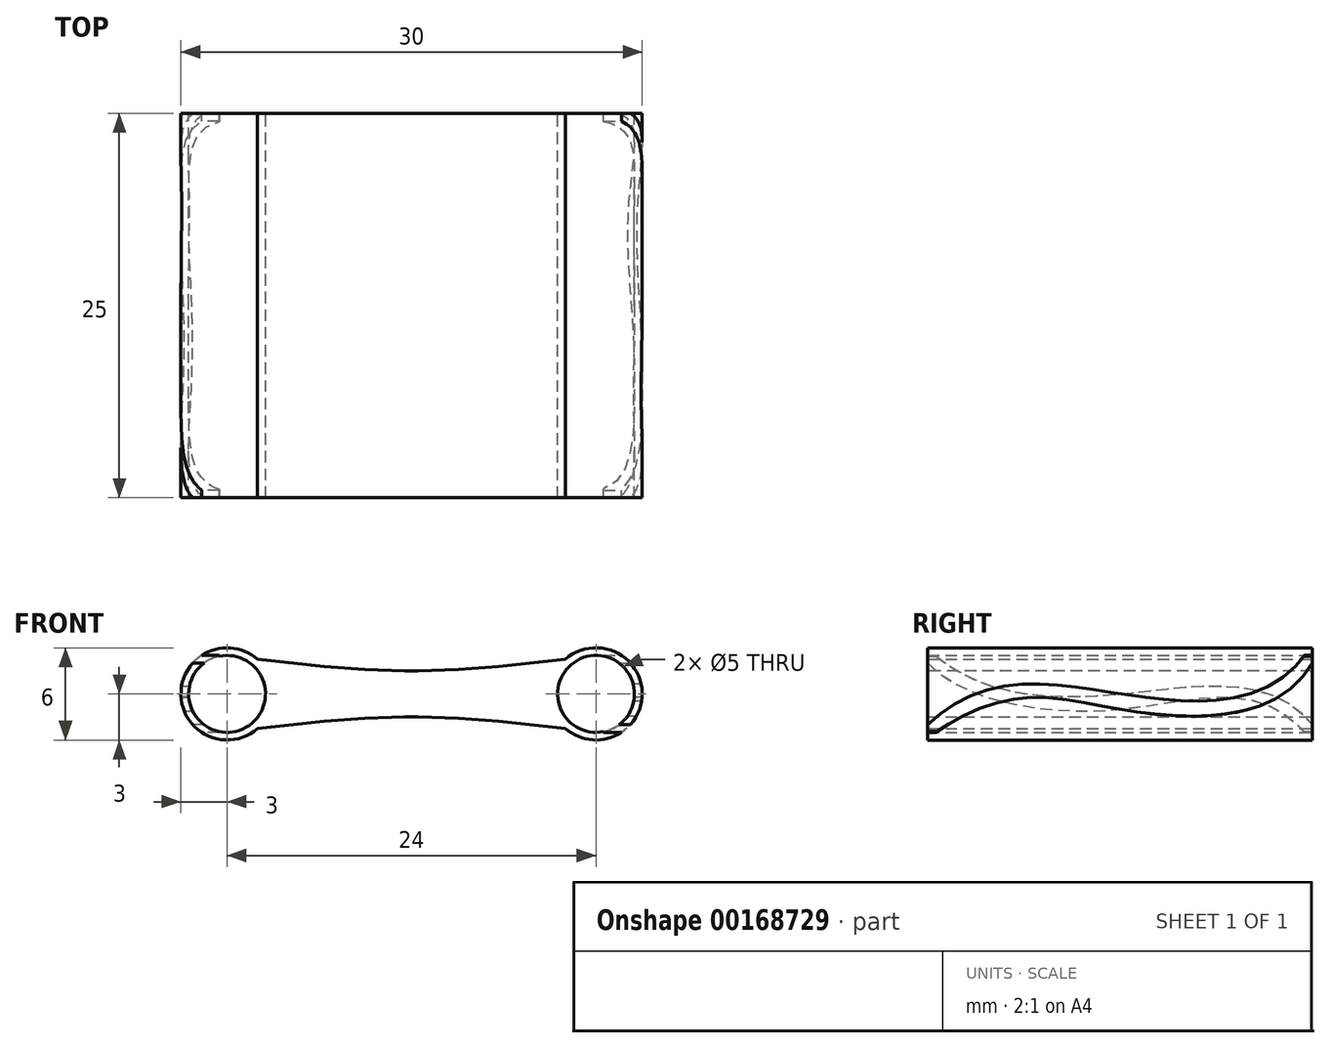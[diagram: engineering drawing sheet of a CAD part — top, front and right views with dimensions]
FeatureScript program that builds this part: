
annotation { "Feature Type Name" : "Feature", "Feature Type Description" : "" }
export const myFeature = defineFeature(function(context is Context, id is Id, definition is map)
    precondition{}
    {
        {
            var Q0;
            Q0=qCreatedBy(makeId("Front.planeOp"),FACE);
            var sketch = newSketch(context, id + "F0", { "sketchPlane" : qUnion([Q0])});
            skPoint(sketch, "E0.middle", {"position": v(0, 0) * mm});
            skCircle(sketch, "E1", {"center": v(12, 0) * mm, "radius": 3 * mm});
            skCircle(sketch, "E2", {"center": v(-12, 0) * mm, "radius": 3 * mm});
            skLineSegment(sketch, "E3", {"start": v(-12, 0) * mm, "end": v(12, 0) * mm, "construction": true});
            skLineSegment(sketch, "E4", {"start": v(-4.98, -1.5) * mm, "end": v(5.72, -1.5) * mm, "construction": true});
            skPoint(sketch, "E5.1.internal.snap0", {"position": v(0.37, -1.5) * mm});
            skLineSegment(sketch, "E6", {"start": v(-10.93, -2.25) * mm, "end": v(10.8, -2.25) * mm, "construction": true});
            skFitSpline(sketch, "E7", {"points": [v(-10.02, -2.25) * mm, v(0, -1.5) * mm, v(10.02, -2.25) * mm], "startDerivative": vector(20.04, 2.26) * mm, "endDerivative": vector(20.04, -2.26) * mm});
            skLineSegment(sketch, "E8", {"start": v(-10.93, 2.25) * mm, "end": v(10.8, 2.25) * mm, "construction": true});
            skLineSegment(sketch, "E9", {"start": v(-4.98, 1.5) * mm, "end": v(5.72, 1.5) * mm, "construction": true});
            skFitSpline(sketch, "E10", {"points": [v(-10.02, 2.25) * mm, v(0, 1.5) * mm, v(10.02, 2.25) * mm], "startDerivative": vector(20.03, -2.25) * mm, "endDerivative": vector(20.03, 2.25) * mm});
            skCircle(sketch, "E11", {"center": v(-12, 0) * mm, "radius": 2.5 * mm});
            skCircle(sketch, "E12", {"center": v(12, 0) * mm, "radius": 2.5 * mm});
            skSolve(sketch);
        }
        {
            var Q0;
            {var subQ0=sQuery(id+"F0.wireOp",EDGE,"E2");var subQ1=sQuery(id+"F0.wireOp",EDGE,"E0.bottom");var subQ2=makeQuery(id+"F0.imprint","INTERSECT",VERTEX,{"derivedFrom":[subQ1,subQ0]});Q0=makeQuery(id+"F0.imprint","IMPRINT",FACE,{"disambiguationData":[TD([[makeQuery(id+"F0.imprint","IMPRINT",EDGE,{"disambiguationData":[TD([[subQ2,-1.0]])],"derivedFrom":subQ1}),-1.0]])]});}
            var Q1;
            {var subQ0=sQuery(id+"F0.wireOp",EDGE,"E7");Q1=makeQuery(id+"F0.imprint","IMPRINT",FACE,{"disambiguationData":[TD([[makeQuery(id+"F0.imprint","IMPRINT",EDGE,{"derivedFrom":subQ0}),1.0]])]});}
            var Q2;
            {var subQ0=sQuery(id+"F0.wireOp",EDGE,"E2");var subQ1=makeQuery(id+"F0.imprint","INTERSECT",VERTEX,{"derivedFrom":[subQ0,sQuery(id+"F0.wireOp",EDGE,"E7")]});Q2=makeQuery(id+"F0.imprint","IMPRINT",FACE,{"disambiguationData":[TD([[makeQuery(id+"F0.imprint","IMPRINT",EDGE,{"disambiguationData":[TD([[subQ1,1.0]])],"derivedFrom":subQ0}),1.0]])]});}
            var Q3;
            {var subQ0=sQuery(id+"F0.wireOp",EDGE,"E1");var subQ1=makeQuery(id+"F0.imprint","INTERSECT",VERTEX,{"derivedFrom":[subQ0,sQuery(id+"F0.wireOp",EDGE,"E7")]});Q3=makeQuery(id+"F0.imprint","IMPRINT",FACE,{"disambiguationData":[TD([[makeQuery(id+"F0.imprint","IMPRINT",EDGE,{"disambiguationData":[TD([[subQ1,1.0]])],"derivedFrom":subQ0}),1.0]])]});}
            extrude(context, id + "F1", {"entities" : qUnion([Q0, Q1, Q2, Q3]), "depth" : 25 * mm, "offsetDistance" : 25 * mm, "symmetric" : true});
        }
        {
            var Q0;
            Q0=qCreatedBy(makeId("Right.planeOp"),FACE);
            var sketch = newSketch(context, id + "F2", { "sketchPlane" : qUnion([Q0])});
            skSolve(sketch);
        }
        {
            var Q0;
            Q0 = qBodyType(qCreatedBy(id + "F2" ,EDGE), BodyType.WIRE);
            var Q1;
            Q1=qCreatedBy(makeId("Right.planeOp"),FACE);
            cPlane(context, id + "F3", {"entities" : qUnion([Q0, Q1]), "cplaneType" : CPlaneType.OFFSET, "offset" : 15 * mm, "width" : 150 * mm, "height" : 150 * mm});
        }
        {
            var Q0;
            Q0=qCreatedBy(id+"F3.planeOp",FACE);
            var sketch = newSketch(context, id + "F4", { "sketchPlane" : qUnion([Q0])});
            skFitSpline(sketch, "E13", {"points": [v(-12.5, -2) * mm, v(0, 0) * mm, v(12.03, 2.54) * mm], "startDerivative": vector(22.83, 21.55) * mm, "endDerivative": vector(16.38, 22.12) * mm});
            skFitSpline(sketch, "E14", {"points": [v(-12, -2.5) * mm, v(0, -1) * mm, v(12.5, 2) * mm], "startDerivative": vector(30.94, 20.46) * mm, "endDerivative": vector(13.56, 23.82) * mm});
            skLineSegment(sketch, "E15.bottom", {"start": v(-12.5, 2.5) * mm, "end": v(12.5, 2.5) * mm});
            skLineSegment(sketch, "E15.top", {"start": v(-12.5, -2.5) * mm, "end": v(12.5, -2.5) * mm});
            skLineSegment(sketch, "E15.left", {"start": v(-12.5, 2.5) * mm, "end": v(-12.5, -2.5) * mm});
            skLineSegment(sketch, "E15.right", {"start": v(12.5, 2.5) * mm, "end": v(12.5, -2.5) * mm});
            skSolve(sketch);
        }
        {
            var Q0;
            {var subQ5=sQuery(id+"F4.wireOp",EDGE,"E13");Q0=makeQuery(id+"F4.imprint","IMPRINT",FACE,{"disambiguationData":[TD([[makeQuery(id+"F4.imprint","IMPRINT",EDGE,{"derivedFrom":subQ5}),-1.0]])]});}
            extrude(context, id + "F5", {"entities" : qUnion([Q0]), "operationType" : NewBodyOperationType.REMOVE, "oppositeDirection" : true, "depth" : 5 * mm, "offsetDistance" : 25 * mm, "symmetric" : true});
        }
        {
            var Q0;
            Q0=qCreatedBy(makeId("Right.planeOp"),FACE);
            var sketch = newSketch(context, id + "F6", { "sketchPlane" : qUnion([Q0])});
            skSolve(sketch);
        }
        {
            var Q0;
            Q0 = qBodyType(qCreatedBy(id + "F6" ,EDGE), BodyType.WIRE);
            var Q1;
            Q1=qCreatedBy(makeId("Right.planeOp"),FACE);
            cPlane(context, id + "F7", {"entities" : qUnion([Q0, Q1]), "cplaneType" : CPlaneType.OFFSET, "offset" : 15 * mm, "oppositeDirection" : true, "width" : 150 * mm, "height" : 150 * mm});
        }
        {
            var Q0;
            Q0=qCreatedBy(id+"F7.planeOp",FACE);
            var sketch = newSketch(context, id + "F8", { "sketchPlane" : qUnion([Q0])});
            skLineSegment(sketch, "E16.bottom", {"start": v(12.5, 2.5) * mm, "end": v(-12.5, 2.5) * mm});
            skLineSegment(sketch, "E16.top", {"start": v(12.5, -2.5) * mm, "end": v(-12.5, -2.5) * mm});
            skLineSegment(sketch, "E16.left", {"start": v(12.5, 2.5) * mm, "end": v(12.5, -2.5) * mm});
            skLineSegment(sketch, "E16.right", {"start": v(-12.5, 2.5) * mm, "end": v(-12.5, -2.5) * mm});
            skPoint(sketch, "E16.middle", {"position": v(0, 0) * mm});
            skFitSpline(sketch, "E17", {"points": [v(12.5, -2) * mm, v(0, 0) * mm, v(-12, 2.5) * mm], "startDerivative": vector(-16.75, 21.21) * mm, "endDerivative": vector(-19.52, 16.36) * mm});
            skFitSpline(sketch, "E18", {"points": [v(12, -2.5) * mm, v(0, -1) * mm, v(-12.5, 2) * mm], "startDerivative": vector(-19.79, 22.4) * mm, "endDerivative": vector(-14.12, 14.88) * mm});
            skSolve(sketch);
        }
        {
            var Q0;
            {var subQ3=sQuery(id+"F8.wireOp",EDGE,"E17");Q0=makeQuery(id+"F8.imprint","IMPRINT",FACE,{"disambiguationData":[TD([[makeQuery(id+"F8.imprint","IMPRINT",EDGE,{"derivedFrom":subQ3}),1.0]])]});}
            extrude(context, id + "F9", {"entities" : qUnion([Q0]), "operationType" : NewBodyOperationType.REMOVE, "depth" : 5 * mm, "offsetDistance" : 25 * mm, "symmetric" : true});
        }
    });
